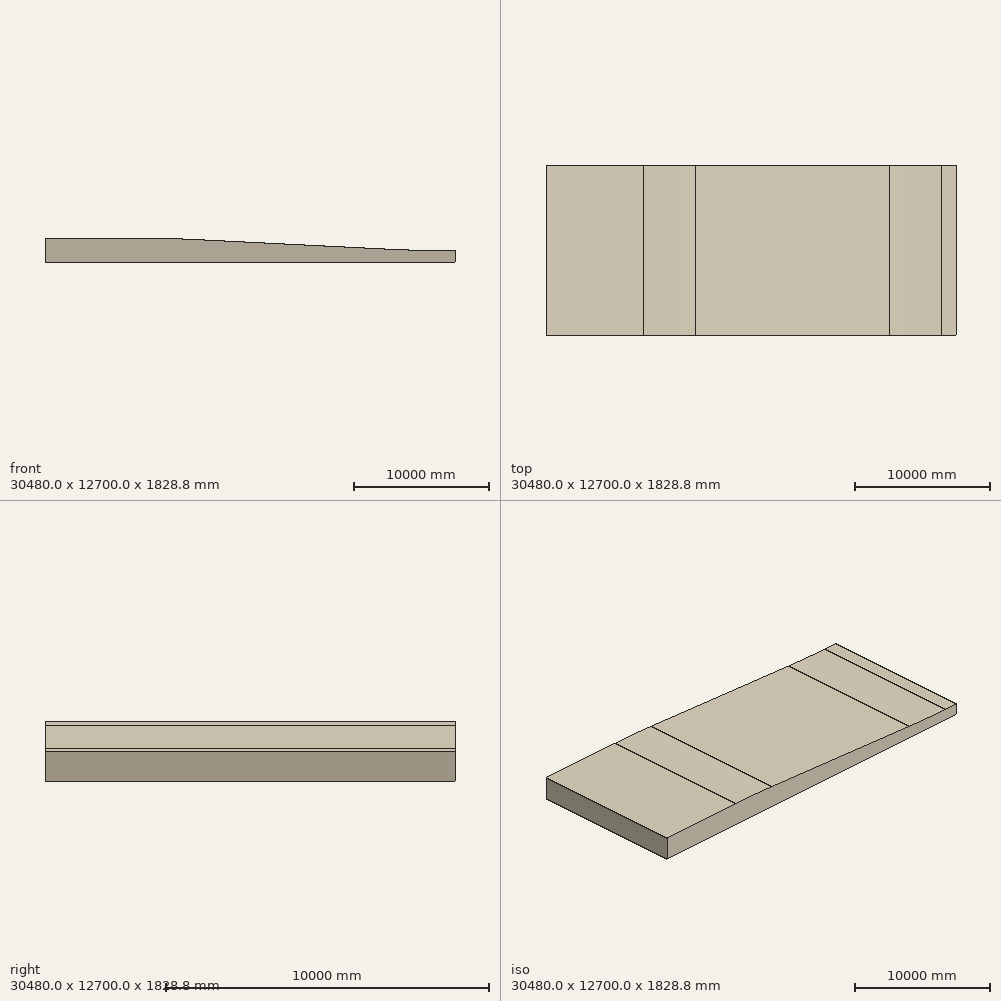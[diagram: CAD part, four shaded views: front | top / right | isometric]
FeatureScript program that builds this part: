
annotation { "Feature Type Name" : "Feature", "Feature Type Description" : "" }
export const myFeature = defineFeature(function(context is Context, id is Id, definition is map)
    precondition{}
    {
        {
            var Q0;
            Q0=qCreatedBy(makeId("Top.planeOp"),FACE);
            var sketch = newSketch(context, id + "F0", { "sketchPlane" : qUnion([Q0])});
            skLineSegment(sketch, "E0.bottom", {"start": v(15240, -6350) * mm, "end": v(-15240, -6350) * mm});
            skLineSegment(sketch, "E0.top", {"start": v(15240, 6350) * mm, "end": v(-15240, 6350) * mm});
            skLineSegment(sketch, "E0.left", {"start": v(15240, -6350) * mm, "end": v(15240, 6350) * mm});
            skLineSegment(sketch, "E0.right", {"start": v(-15240, -6350) * mm, "end": v(-15240, 6350) * mm});
            skPoint(sketch, "E0.middle", {"position": v(0, 0) * mm});
            skSolve(sketch);
        }
        {
            var Q0;
            Q0=makeQuery(id+"F0.imprint","IMPRINT",FACE,{"disambiguationData":[TD([[makeQuery(id+"F0.imprint","IMPRINT",EDGE,{"derivedFrom":sQuery(id+"F0.wireOp",EDGE,"E0.bottom")}),-1.0]])]});
            extrude(context, id + "F1", {"entities" : qUnion([Q0]), "depth" : 1828.8 * mm});
        }
        {
            var Q0;
            Q0=makeQuery(id+"F1.opExtrude","SWEPT_FACE",FACE,{"disambiguationData":[OSD([sQuery(id+"F0.wireOp",EDGE,"E0.bottom")])]});
            var sketch = newSketch(context, id + "F2", { "sketchPlane" : qUnion([Q0])});
            skPoint(sketch, "E1.visualSharp", {"position": v(-6096, 1828.8) * mm});
            skLineSegment(sketch, "E2", {"start": v(-15240, 1828.8) * mm, "end": v(-15240, 7285.99) * mm});
            skLineSegment(sketch, "E3", {"start": v(-15240, 7285.99) * mm, "end": v(15240, 7285.99) * mm});
            skLineSegment(sketch, "E4", {"start": v(-15240, 1828.8) * mm, "end": v(-7999.81, 1828.8) * mm});
            skLineSegment(sketch, "E5", {"start": v(-4194.56, 1733.73) * mm, "end": v(10290.56, 1009.47) * mm});
            skLineSegment(sketch, "E6", {"start": v(14095.81, 914.4) * mm, "end": v(15240, 914.4) * mm});
            skLineSegment(sketch, "E7", {"start": v(15240, 914.4) * mm, "end": v(15240, 7285.99) * mm});
            skArc(sketch, "E8.filletArc", {"start": v(-4194.56, 1733.73) * mm, "mid": v(-6096.6, 1805.03) * mm, "end": v(-7999.81, 1828.8) * mm});
            skPoint(sketch, "E9.visualSharp", {"position": v(12192, 914.4) * mm});
            skArc(sketch, "E9.filletArc", {"start": v(10290.56, 1009.47) * mm, "mid": v(12192.6, 938.17) * mm, "end": v(14095.81, 914.4) * mm});
            skSolve(sketch);
        }
        {
            var Q0;
            Q0 = qSketchRegion(id + "F2", true);
            extrude(context, id + "F3", {"entities" : qUnion([Q0]), "operationType" : NewBodyOperationType.REMOVE, "endBound" : BoundingType.THROUGH_ALL, "oppositeDirection" : true, "depth" : 7620 * mm});
        }
    });
